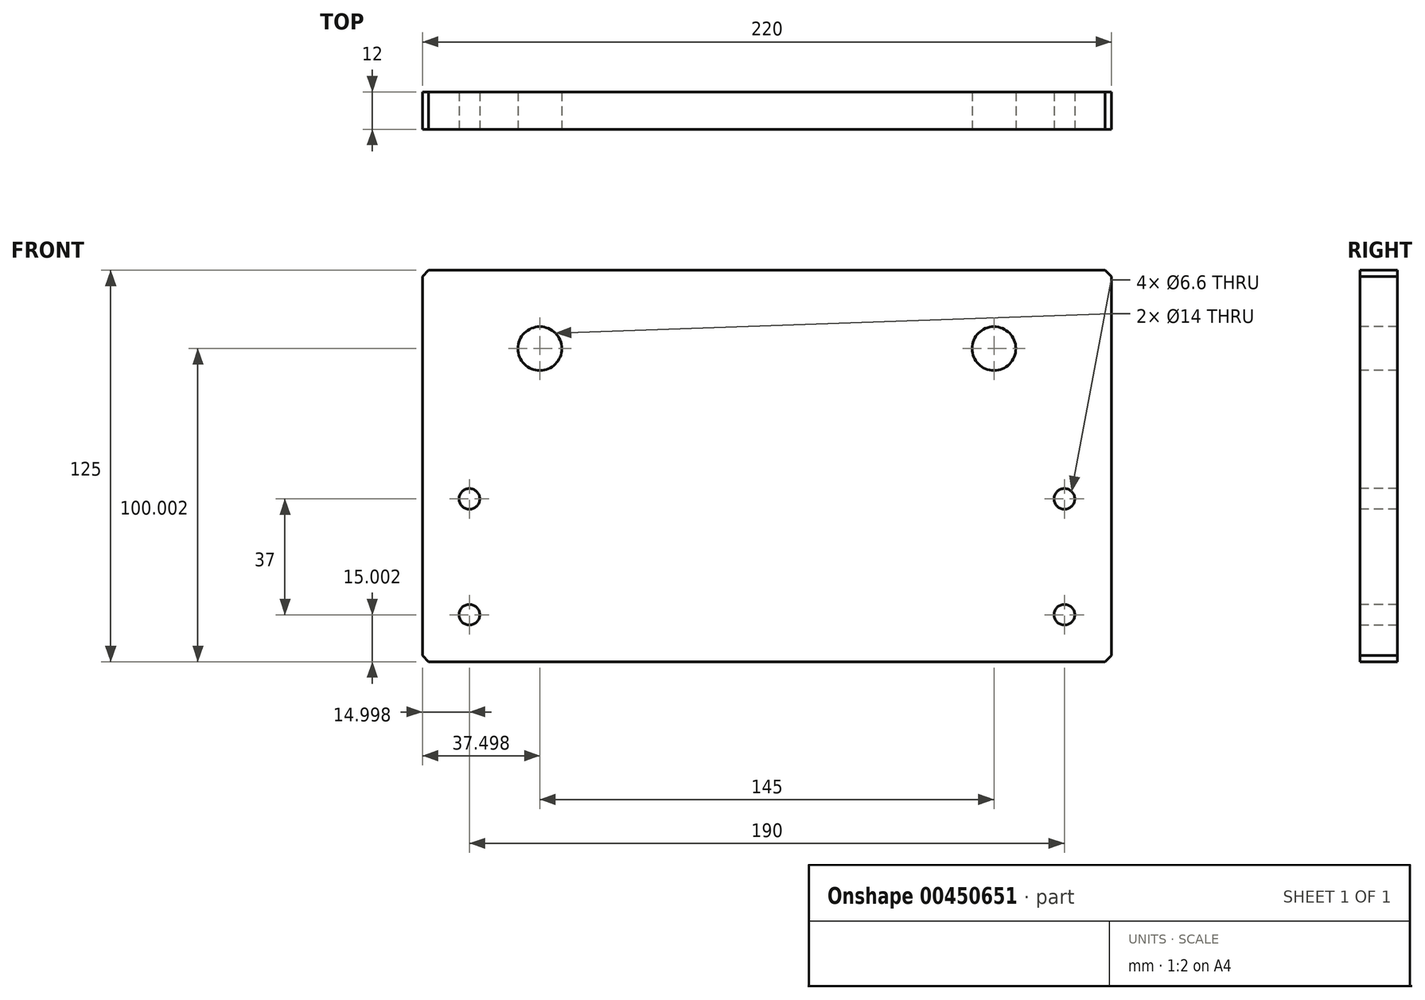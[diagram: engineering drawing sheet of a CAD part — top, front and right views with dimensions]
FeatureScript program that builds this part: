
annotation { "Feature Type Name" : "Feature", "Feature Type Description" : "" }
export const myFeature = defineFeature(function(context is Context, id is Id, definition is map)
    precondition{}
    {
        {
            var Q0;
            Q0=qCreatedBy(makeId("Front.planeOp"),FACE);
            var sketch = newSketch(context, id + "F0", { "sketchPlane" : qUnion([Q0])});
            skLineSegment(sketch, "E0", {"start": v(94.71, 33.45) * mm, "end": v(126.64, 33.45) * mm});
            skLineSegment(sketch, "E1", {"start": v(104.55, 58.45) * mm, "end": v(116.55, 58.45) * mm});
            skLineSegment(sketch, "E2", {"start": v(104.55, -66.55) * mm, "end": v(116.55, -66.55) * mm});
            skLineSegment(sketch, "E3", {"start": v(104.55, -66.55) * mm, "end": v(104.55, 58.45) * mm});
            skLineSegment(sketch, "E4", {"start": v(116.55, -66.55) * mm, "end": v(116.55, 58.45) * mm});
            skLineSegment(sketch, "E5", {"start": v(19.49, -66.55) * mm, "end": v(-196.51, -66.55) * mm});
            skLineSegment(sketch, "E6", {"start": v(21.49, -64.55) * mm, "end": v(19.49, -66.55) * mm});
            skLineSegment(sketch, "E7", {"start": v(19.49, 58.45) * mm, "end": v(-196.51, 58.45) * mm});
            skLineSegment(sketch, "E8", {"start": v(21.49, 56.45) * mm, "end": v(19.49, 58.45) * mm});
            skLineSegment(sketch, "E9", {"start": v(21.49, 56.45) * mm, "end": v(21.49, -64.55) * mm});
            skLineSegment(sketch, "E10", {"start": v(-198.51, 56.45) * mm, "end": v(-198.51, -64.55) * mm});
            skLineSegment(sketch, "E11", {"start": v(-196.51, -66.55) * mm, "end": v(-198.51, -64.55) * mm});
            skLineSegment(sketch, "E12", {"start": v(-196.51, 58.45) * mm, "end": v(-198.51, 56.45) * mm});
            skLineSegment(sketch, "E13", {"start": v(1.94, -14.55) * mm, "end": v(11.04, -14.55) * mm});
            skLineSegment(sketch, "E14", {"start": v(6.49, -19.1) * mm, "end": v(6.49, -10) * mm});
            skLineSegment(sketch, "E15", {"start": v(6.49, -47) * mm, "end": v(6.49, -56.1) * mm});
            skLineSegment(sketch, "E16", {"start": v(1.94, -51.55) * mm, "end": v(11.04, -51.55) * mm});
            skLineSegment(sketch, "E17", {"start": v(-183.51, -47) * mm, "end": v(-183.51, -56.1) * mm});
            skLineSegment(sketch, "E18", {"start": v(-188.06, -51.55) * mm, "end": v(-178.96, -51.55) * mm});
            skLineSegment(sketch, "E19", {"start": v(-183.51, -19.1) * mm, "end": v(-183.51, -10) * mm});
            skLineSegment(sketch, "E20", {"start": v(-178.96, -14.55) * mm, "end": v(-188.06, -14.55) * mm});
            skCircle(sketch, "E21", {"center": v(-16.01, 33.45) * mm, "radius": 7 * mm});
            skLineSegment(sketch, "E22", {"start": v(-16.01, 42.55) * mm, "end": v(-16.01, 24.35) * mm});
            skLineSegment(sketch, "E23", {"start": v(-25.11, 33.45) * mm, "end": v(-6.91, 33.45) * mm});
            skCircle(sketch, "E24", {"center": v(-161.01, 33.45) * mm, "radius": 7 * mm});
            skLineSegment(sketch, "E25", {"start": v(-161.01, 42.55) * mm, "end": v(-161.01, 24.35) * mm});
            skLineSegment(sketch, "E26", {"start": v(-170.11, 33.45) * mm, "end": v(-151.91, 33.45) * mm});
            skLineSegment(sketch, "E27", {"start": v(94.71, -14.55) * mm, "end": v(126.64, -14.55) * mm});
            skLineSegment(sketch, "E28", {"start": v(94.71, -51.55) * mm, "end": v(126.64, -51.55) * mm});
            skCircle(sketch, "E29", {"center": v(6.49, -51.55) * mm, "radius": 3.3 * mm});
            skCircle(sketch, "E30", {"center": v(6.49, -14.55) * mm, "radius": 3.3 * mm});
            skCircle(sketch, "E31", {"center": v(-183.51, -14.55) * mm, "radius": 3.3 * mm});
            skCircle(sketch, "E32", {"center": v(-183.51, -51.55) * mm, "radius": 3.3 * mm});
            skSolve(sketch);
        }
        {
            var Q0;
            Q0=makeQuery(id+"F0.imprint","IMPRINT",FACE,{"disambiguationData":[TD([[makeQuery(id+"F0.imprint","IMPRINT",EDGE,{"derivedFrom":sQuery(id+"F0.wireOp",EDGE,"E5")}),-1.0]])]});
            extrude(context, id + "F1", {"entities" : qUnion([Q0]), "oppositeDirection" : true, "depth" : 12 * mm});
        }
    });
